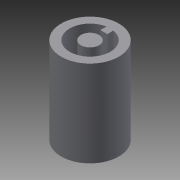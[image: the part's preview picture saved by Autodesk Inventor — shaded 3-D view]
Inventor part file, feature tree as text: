
AUTODESK INVENTOR PART (.ipt)
format: ipt  version: 2013 SP2 (Build 170200200, 200)  size: 130,560 bytes
history: native  units: in
note: dims shown in document units (in); Inventor stores cm internally (conversion verified against a paired STEP export)
features: extrude x6, sketch x5
ambient origin geometry x8: Origin, YZ Plane, XZ Plane, XY Plane, X Axis, Y Axis, Z Axis, Center Point
feature tree (11):
  extrude  "Extrusion2"  Depth=0.3307in
  extrude  "Extrusion3"  Depth=0.1732in
  extrude  "Extrusion4"  Depth=0.388in
  extrude  "Extrusion5"  Depth=0.4724in TaperAngle=0.0deg
  extrude  "Extrusion6"  Depth=0.388in
  extrude  "Extrusion7"  Depth=0.33in TaperAngle=0.0deg
  sketch  "Sketch1"  dims[d5=0.5512in d8=0.3307in]
  sketch  "Sketch3"  dims[d9=0.3543in d10=0.0in d11=0.1732in]
  sketch  "Sketch5"  dims[d12=0.4724in d13=0.0in d14=0.388in]
  sketch  "Sketch6"  dims[d15=0.4724in d16=0.0in d17=0.4724in d18=0.0394in d19=0.0in d20=0.0in]
  sketch  "Sketch7"  dims[d21=0.3543in d22=0.0in d37=0.388in d38=0.33in d39=0.0in]
